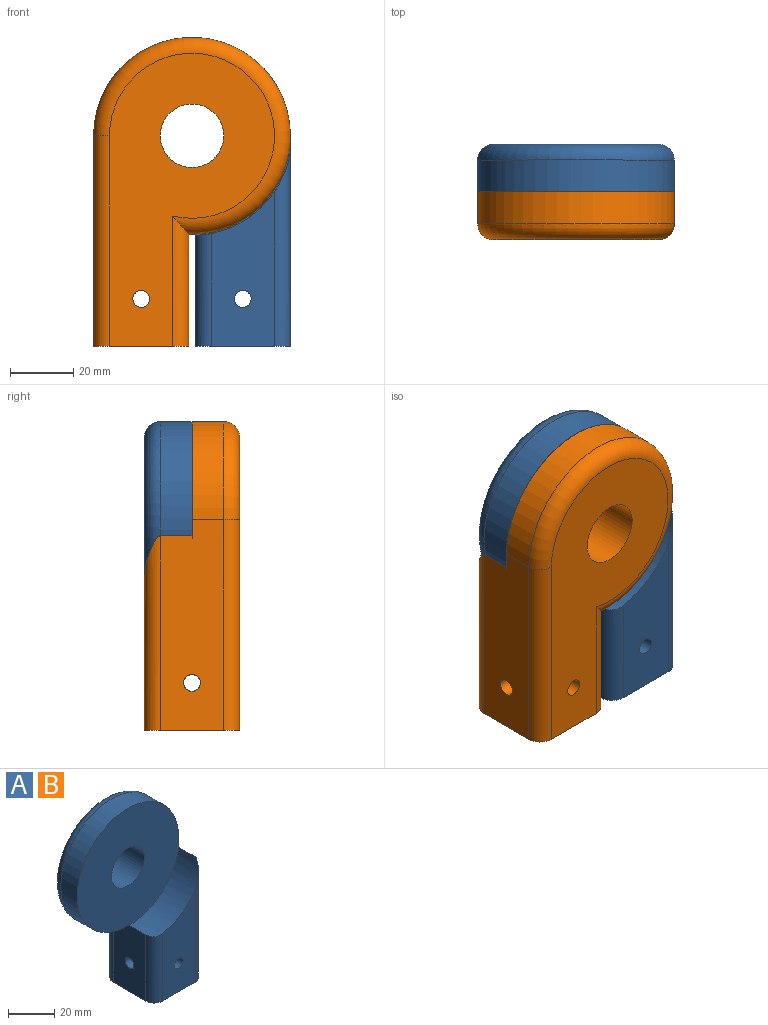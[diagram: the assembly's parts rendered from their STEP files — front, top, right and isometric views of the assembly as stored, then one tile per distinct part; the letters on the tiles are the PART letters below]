
ASSEMBLY  parts=2 mates=1
PART A: 23 faces, bbox 67.1x30x100 mm
  f0: plane 62.4x62mm, normal (0,-1,0), area 2723.5mm2, adj f4,f5,f13,f14,f15
  f1: plane 30x20.3mm, normal (1,0,0), area 586.9mm2, adj f2,f6,f10,f12,f16
  f2: plane 20.3x20.3mm, normal (0,0,-1), area 412.1mm2, adj f1,f3,f10,f12
  f3: plane 30x20.3mm, normal (-1,0,0), area 586.9mm2, adj f2,f6,f10,f12,f17
  f4: plane 66.4x20mm, normal (1,0,0), area 1255mm2, adj f0,f6,f13,f15,f17,f18,f22
  f5: plane 35.42x20mm, normal (-1,0,0), area 682.1mm2, adj f0,f6,f13,f15,f16,f19,f21
  f6: plane 30x30mm, normal (0,0,-1), area 466.4mm2, adj f1,f3,f4,f5,f7,f8,f10,f12
  f7: plane 48.77x20mm, normal (0,-1,0), area 783mm2, adj f6,f11,f15,f21,f22
  f8: plane 92.4x52mm, normal (0,1,0), area 2739.2mm2, adj f6,f9,f14,f18,f19,f20
  f9: cylinder r=2.65mm len=5.3mm, axis (0,1,0), area 80.8mm2, adj f8,f10
  f10: plane 30x20.3mm, normal (0,-1,0), area 586.9mm2, adj f1,f2,f3,f6,f9
  f11: cylinder r=2.65mm len=5.3mm, axis (0,1,0), area 80.8mm2, adj f7,f12
  f12: plane 30x20.3mm, normal (0,1,0), area 586.9mm2, adj f1,f2,f3,f6,f11
  f13: cylinder r=31mm len=62mm, axis (0,1,0), area 1470.8mm2, adj f0,f4,f5,f20
  f14: cylinder r=10mm len=20mm, axis (0,1,0), area 942.5mm2, adj f0,f8
  f15: cylinder r=31.42mm len=30mm, axis (0,1,0), area 623.1mm2, adj f0,f4,f5,f7,f21,f22
  f16: cylinder r=2.65mm len=5.3mm, axis (1,0,0), area 80.8mm2, adj f1,f5
  f17: cylinder r=2.65mm len=5.3mm, axis (1,0,0), area 80.8mm2, adj f3,f4
  f18: cylinder r=5mm len=66.4mm, axis (0,0,1), area 521.5mm2, adj f4,f6,f8,f20
  f19: cylinder r=5mm len=41.1mm, axis (0,0,-1), area 293.8mm2, adj f5,f6,f8,f20
  f20: torus R=26mm, axis (0,-1,0), area 1102.3mm2, adj f8,f13,f18,f19
  f21: cylinder r=5mm len=35.56mm, axis (0,0,1), area 276.1mm2, adj f5,f6,f7,f15
  f22: cylinder r=5mm len=61.31mm, axis (0,0,-1), area 436.5mm2, adj f4,f6,f7,f15
PART B: same geometry as A
PLACE A t=(77.06,31.77,26.16)mm
PLACE B rot(axis=(0,0,-1),180deg) t=(77.06,1.77,26.16)mm
MATE revolute A.f14 <-> B.f14  axis (0,-1,0) through (77.06,16.77,26.16)mm
